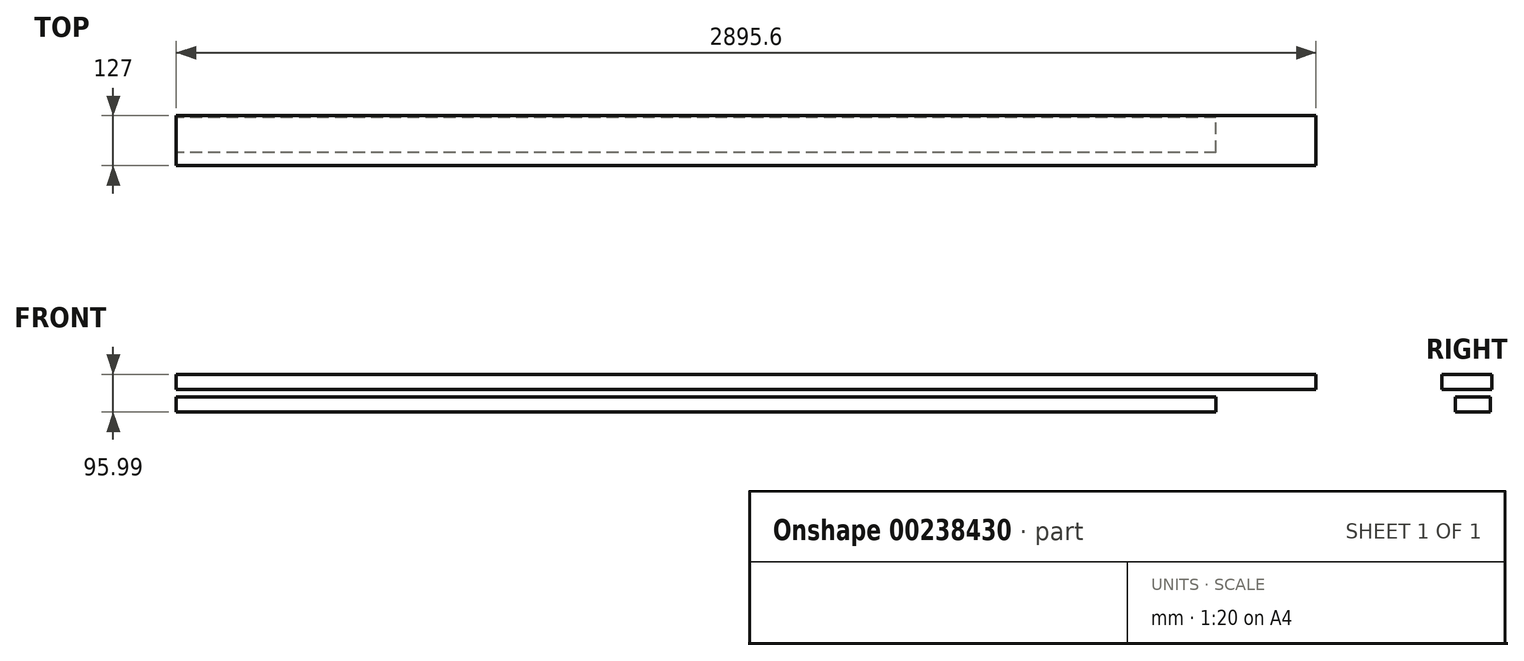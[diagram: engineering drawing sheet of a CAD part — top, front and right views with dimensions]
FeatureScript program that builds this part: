
annotation { "Feature Type Name" : "Feature", "Feature Type Description" : "" }
export const myFeature = defineFeature(function(context is Context, id is Id, definition is map)
    precondition{}
    {
        {
            var Q0;
            Q0=qCreatedBy(makeId("Right.planeOp"),FACE);
            var sketch = newSketch(context, id + "F0", { "sketchPlane" : qUnion([Q0])});
            skLineSegment(sketch, "E0.bottom", {"start": v(-42.75, 0) * mm, "end": v(46.15, 0) * mm});
            skLineSegment(sketch, "E0.top", {"start": v(-42.75, -38.1) * mm, "end": v(46.15, -38.1) * mm});
            skLineSegment(sketch, "E0.left", {"start": v(-42.75, 0) * mm, "end": v(-42.75, -38.1) * mm});
            skLineSegment(sketch, "E0.right", {"start": v(46.15, 0) * mm, "end": v(46.15, -38.1) * mm});
            skSolve(sketch);
        }
        {
            var Q0;
            Q0 = qSketchRegion(id + "F0", true);
            extrude(context, id + "F1", {"entities" : qUnion([Q0]), "depth" : 2641.6 * mm});
        }
        {
            var Q0;
            Q0=qCreatedBy(makeId("Right.planeOp"),FACE);
            var sketch = newSketch(context, id + "F2", { "sketchPlane" : qUnion([Q0])});
            skLineSegment(sketch, "E1.bottom", {"start": v(-76.81, 57.9) * mm, "end": v(50.19, 57.9) * mm});
            skLineSegment(sketch, "E1.top", {"start": v(-76.81, 19.8) * mm, "end": v(50.19, 19.8) * mm});
            skLineSegment(sketch, "E1.left", {"start": v(-76.81, 57.9) * mm, "end": v(-76.81, 19.8) * mm});
            skLineSegment(sketch, "E1.right", {"start": v(50.19, 57.9) * mm, "end": v(50.19, 19.8) * mm});
            skSolve(sketch);
        }
        {
            var Q0;
            Q0=makeQuery(id+"F2.imprint","IMPRINT",FACE,{"disambiguationData":[TD([[makeQuery(id+"F2.imprint","IMPRINT",EDGE,{"derivedFrom":sQuery(id+"F2.wireOp",EDGE,"E1.bottom")}),-1.0]])]});
            extrude(context, id + "F3", {"entities" : qUnion([Q0]), "depth" : 2895.6 * mm});
        }
    });
